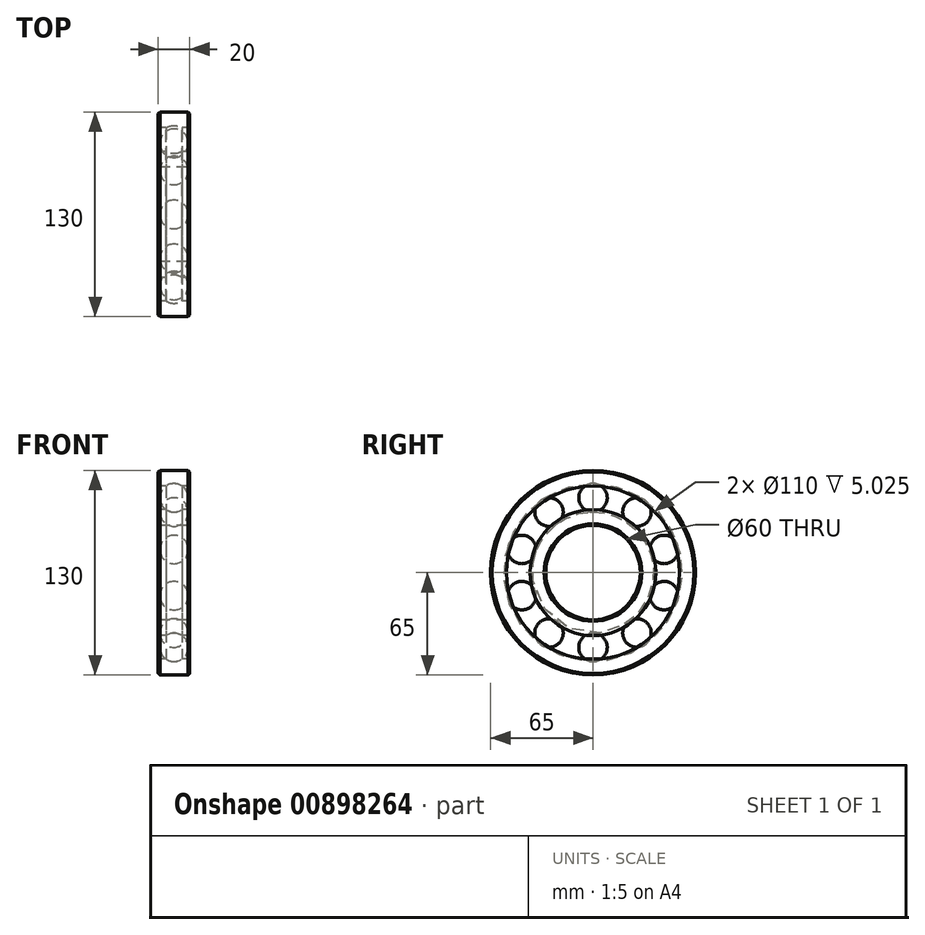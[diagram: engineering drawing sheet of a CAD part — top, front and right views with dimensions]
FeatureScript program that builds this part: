
annotation { "Feature Type Name" : "Feature", "Feature Type Description" : "" }
export const myFeature = defineFeature(function(context is Context, id is Id, definition is map)
    precondition{}
    {
        {
            var Q0;
            Q0=qCreatedBy(makeId("Front.planeOp"),FACE);
            var sketch = newSketch(context, id + "F0", { "sketchPlane" : qUnion([Q0])});
            skLineSegment(sketch, "E0.bottom", {"start": v(10, 55) * mm, "end": v(4.97, 55) * mm});
            skLineSegment(sketch, "E0.top", {"start": v(10, 65) * mm, "end": v(-10, 65) * mm});
            skLineSegment(sketch, "E0.left", {"start": v(10, 65) * mm, "end": v(10, 55) * mm});
            skLineSegment(sketch, "E0.right", {"start": v(-10, 65) * mm, "end": v(-10, 55) * mm});
            skPoint(sketch, "E0.middle", {"position": v(0, 60) * mm});
            skLineSegment(sketch, "E1.bottom", {"start": v(10, 30) * mm, "end": v(-10, 30) * mm});
            skLineSegment(sketch, "E1.top", {"start": v(10, 40) * mm, "end": v(4.97, 40) * mm});
            skLineSegment(sketch, "E1.left", {"start": v(10, 40) * mm, "end": v(10, 30) * mm});
            skLineSegment(sketch, "E1.right", {"start": v(-10, 40) * mm, "end": v(-10, 30) * mm});
            skPoint(sketch, "E1.middle", {"position": v(0, 35) * mm});
            skLineSegment(sketch, "E2", {"start": v(-16.1, 0) * mm, "end": v(20.56, 0) * mm, "construction": true});
            skLineSegment(sketch, "E3", {"start": v(0, 60) * mm, "end": v(0, 35) * mm, "construction": true});
            skArc(sketch, "E4", {"start": v(-4.97, 40) * mm, "mid": v(0, 38.5) * mm, "end": v(4.97, 40) * mm});
            skArc(sketch, "E5.trimOffspring", {"start": v(4.97, 55) * mm, "mid": v(0, 56.5) * mm, "end": v(-4.97, 55) * mm});
            skLineSegment(sketch, "E6.trimOffspring", {"start": v(-4.97, 40) * mm, "end": v(-10, 40) * mm});
            skLineSegment(sketch, "E7.trimOffspring", {"start": v(-4.97, 55) * mm, "end": v(-10, 55) * mm});
            skSolve(sketch);
        }
        {
            var Q0;
            Q0=makeQuery(id+"F0.imprint","IMPRINT",FACE,{"disambiguationData":[TD([[makeQuery(id+"F0.imprint","IMPRINT",EDGE,{"derivedFrom":sQuery(id+"F0.wireOp",EDGE,"E0.bottom")}),-1.0]])]});
            var Q1;
            Q1=makeQuery(id+"F0.imprint","IMPRINT",FACE,{"disambiguationData":[TD([[makeQuery(id+"F0.imprint","IMPRINT",EDGE,{"derivedFrom":sQuery(id+"F0.wireOp",EDGE,"E1.bottom")}),-1.0]])]});
            var Q2;
            Q2=sQuery(id+"F0.wireOp",EDGE,"E2");
            revolve(context, id + "F1", {"surfaceOperationType" : NewSurfaceOperationType.NEW, "entities" : qUnion([Q0, Q1]), "axis" : qUnion([Q2]), "revolveType" : RevolveType.FULL});
        }
        {
            var Q0;
            Q0=qCreatedBy(makeId("Front.planeOp"),FACE);
            var sketch = newSketch(context, id + "F2", { "sketchPlane" : qUnion([Q0])});
            skArc(sketch, "E8", {"start": v(9.05, 47.5) * mm, "mid": v(0, 56.55) * mm, "end": v(-9.05, 47.5) * mm});
            skLineSegment(sketch, "E9", {"start": v(-9.05, 47.5) * mm, "end": v(9.05, 47.5) * mm});
            skSolve(sketch);
        }
        {
            var Q0;
            Q0=makeQuery(id+"F2.imprint","IMPRINT",FACE,{"disambiguationData":[TD([[makeQuery(id+"F2.imprint","IMPRINT",EDGE,{"derivedFrom":sQuery(id+"F2.wireOp",EDGE,"E8")}),1.0]])]});
            var Q1;
            Q1=sQuery(id+"F2.wireOp",EDGE,"E9");
            revolve(context, id + "F3", {"surfaceOperationType" : NewSurfaceOperationType.NEW, "entities" : qUnion([Q0]), "axis" : qUnion([Q1]), "revolveType" : RevolveType.FULL});
        }
        {
            var Q0;
            Q0=makeQuery(id+"F3.opRevolve","SWEPT_BODY",BODY,{"disambiguationData":[OSD([sQuery(id+"F2.wireOp",EDGE,"E8"),sQuery(id+"F2.wireOp",EDGE,"E9")])]});
            var Q1;
            Q1=makeQuery(id+"F1.opRevolve","SWEPT_EDGE",EDGE,{"disambiguationData":[OSD([sQuery(id+"F0.wireOp",EDGE,"E1.bottom"),sQuery(id+"F0.wireOp",EDGE,"E1.left")])]});
            circularPattern(context, id + "F4", {"entities" : qUnion([Q0]), "axis" : qUnion([Q1]), "angle" : 360 * degree, "instanceCount" : 10, "equalSpace" : true});
        }
        {
            var Q0;
            Q0=makeQuery(id+"F1.opRevolve","SWEPT_EDGE",EDGE,{"disambiguationData":[OSD([sQuery(id+"F0.wireOp",EDGE,"E1.bottom"),sQuery(id+"F0.wireOp",EDGE,"E1.left")])]});
            var Q1;
            Q1=makeQuery(id+"F1.opRevolve","SWEPT_EDGE",EDGE,{"disambiguationData":[OSD([sQuery(id+"F0.wireOp",EDGE,"E1.bottom"),sQuery(id+"F0.wireOp",EDGE,"E1.right")])]});
            var Q2;
            Q2=makeQuery(id+"F1.opRevolve","SWEPT_EDGE",EDGE,{"disambiguationData":[OSD([sQuery(id+"F0.wireOp",EDGE,"E0.top"),sQuery(id+"F0.wireOp",EDGE,"E0.right")])]});
            var Q3;
            Q3=makeQuery(id+"F1.opRevolve","SWEPT_EDGE",EDGE,{"disambiguationData":[OSD([sQuery(id+"F0.wireOp",EDGE,"E0.top"),sQuery(id+"F0.wireOp",EDGE,"E0.left")])]});
            chamfer(context, id + "F5", {"entities" : qUnion([Q0, Q1, Q2, Q3]), "width" : 1 * mm, "tangentPropagation" : true});
        }
    });
